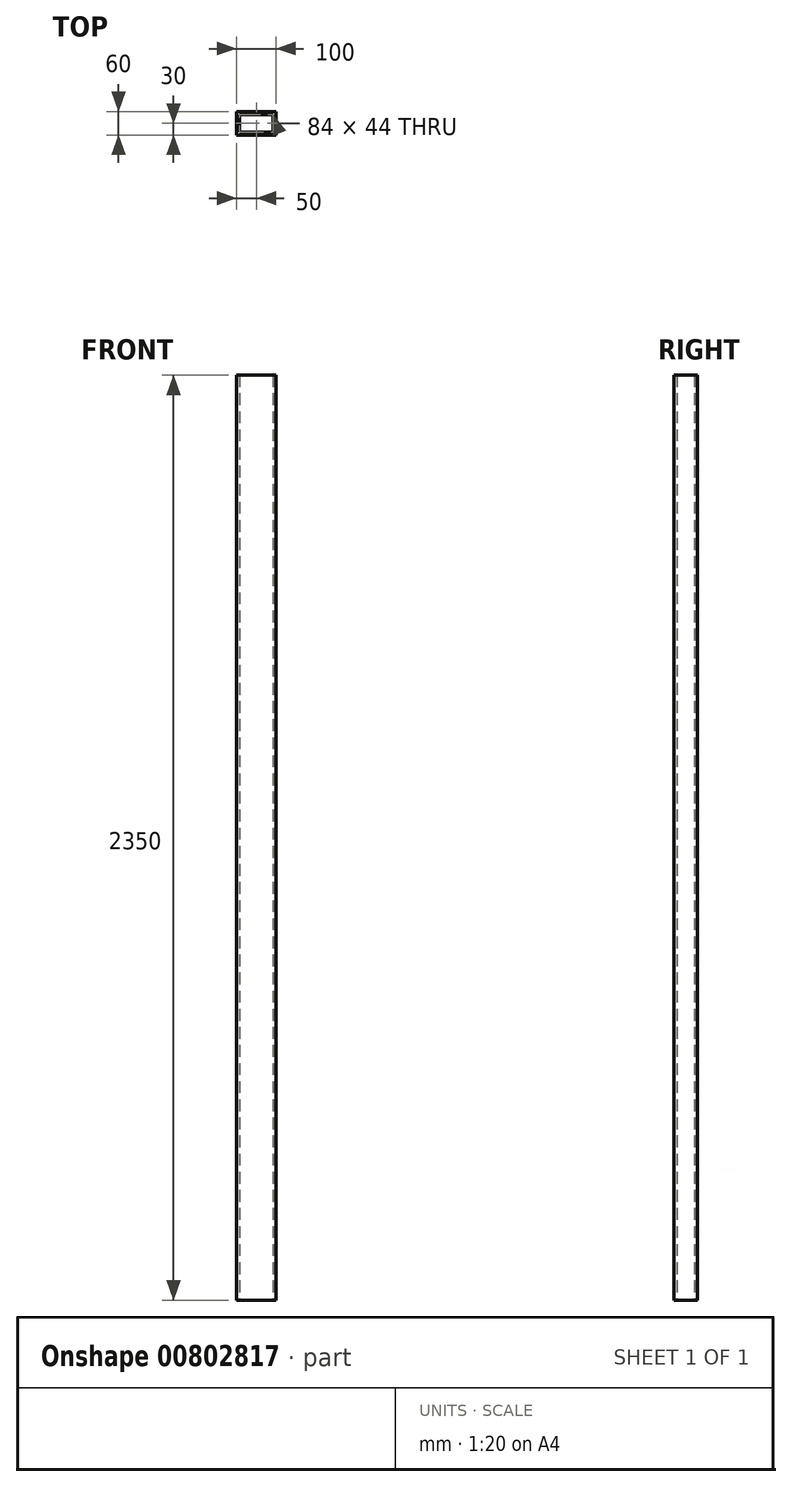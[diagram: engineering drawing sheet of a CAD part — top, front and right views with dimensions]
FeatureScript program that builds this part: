
annotation { "Feature Type Name" : "Feature", "Feature Type Description" : "" }
export const myFeature = defineFeature(function(context is Context, id is Id, definition is map)
    precondition{}
    {
        {
            var Q0;
            Q0=qCreatedBy(makeId("Top.planeOp"),FACE);
            var sketch = newSketch(context, id + "F0", { "sketchPlane" : qUnion([Q0])});
            skLineSegment(sketch, "E0.bottom", {"start": v(50, -30) * mm, "end": v(-50, -30) * mm});
            skLineSegment(sketch, "E0.top", {"start": v(50, 30) * mm, "end": v(-50, 30) * mm});
            skLineSegment(sketch, "E0.left", {"start": v(50, -30) * mm, "end": v(50, 30) * mm});
            skLineSegment(sketch, "E0.right", {"start": v(-50, -30) * mm, "end": v(-50, 30) * mm});
            skPoint(sketch, "E0.middle", {"position": v(0, 0) * mm});
            skLineSegment(sketch, "E1.0", {"start": v(42, 22) * mm, "end": v(-42, 22) * mm});
            skLineSegment(sketch, "E1.1", {"start": v(42, -22) * mm, "end": v(42, 22) * mm});
            skLineSegment(sketch, "E1.2", {"start": v(42, -22) * mm, "end": v(-42, -22) * mm});
            skLineSegment(sketch, "E1.3", {"start": v(-42, -22) * mm, "end": v(-42, 22) * mm});
            skSolve(sketch);
        }
        {
            var Q0;
            Q0 = qSketchRegion(id + "F0", true);
            extrude(context, id + "F1", {"entities" : qUnion([Q0]), "depth" : 2350 * mm, "offsetDistance" : 25 * mm});
        }
    });
